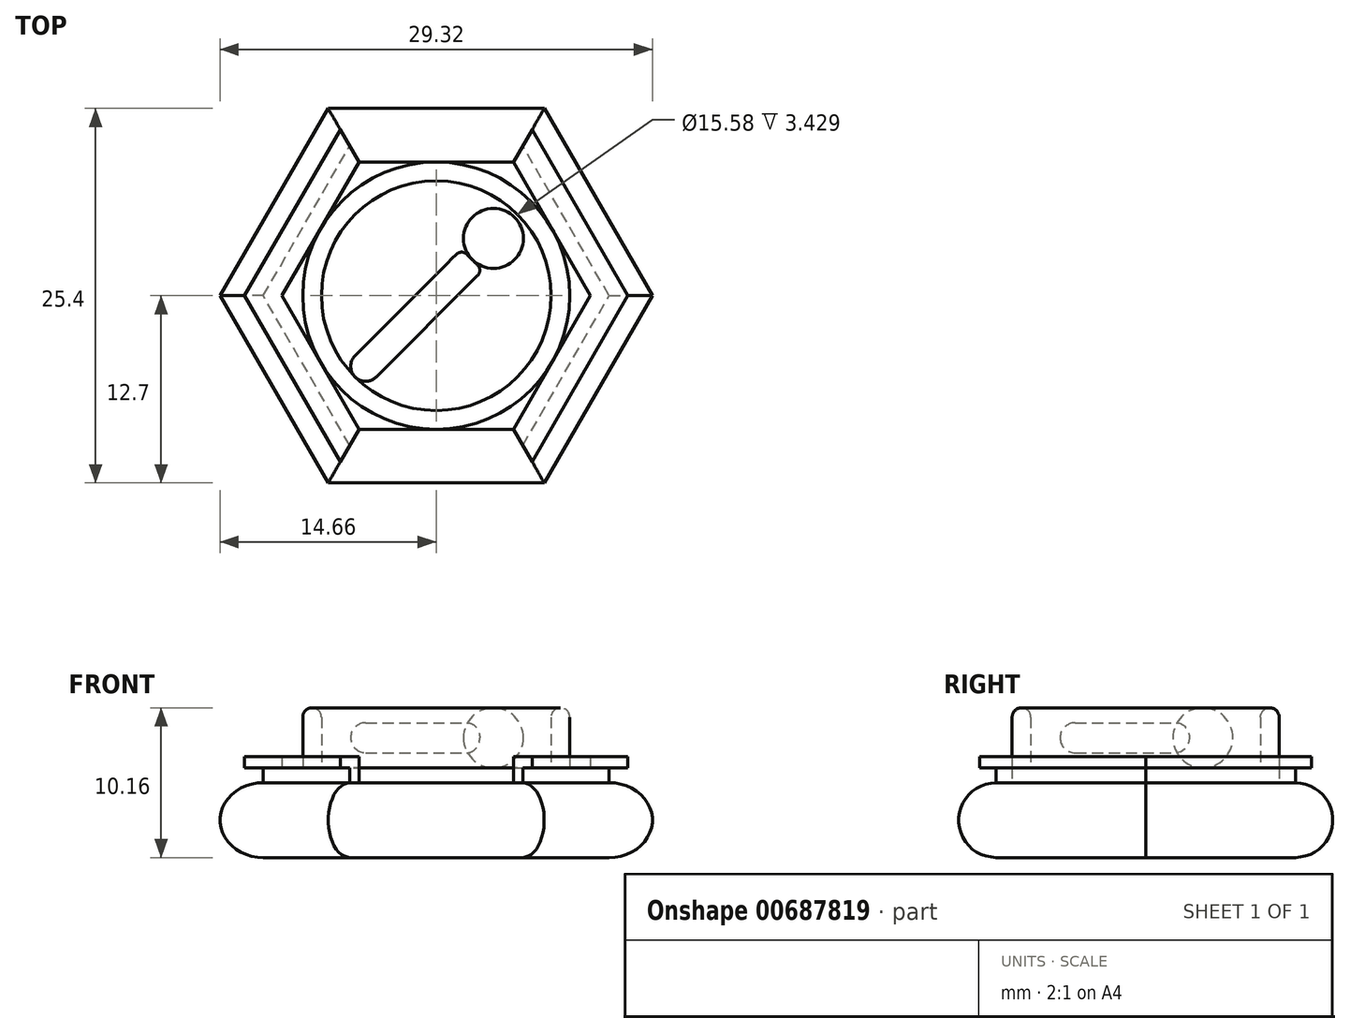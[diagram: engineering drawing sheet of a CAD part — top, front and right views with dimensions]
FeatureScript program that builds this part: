
annotation { "Feature Type Name" : "Feature", "Feature Type Description" : "" }
export const myFeature = defineFeature(function(context is Context, id is Id, definition is map)
    precondition{}
    {
        {
            var Q0;
            Q0=qCreatedBy(makeId("Front.planeOp"),FACE);
            var sketch = newSketch(context, id + "F0", { "sketchPlane" : qUnion([Q0])});
            skLineSegment(sketch, "E0", {"start": v(0, 0) * mm, "end": v(-12.7, 0) * mm});
            skLineSegment(sketch, "E1", {"start": v(-12.7, 0) * mm, "end": v(-12.7, 5.08) * mm, "construction": true});
            skLineSegment(sketch, "E2", {"start": v(12.7, 5.08) * mm, "end": v(12.7, 0) * mm, "construction": true});
            skLineSegment(sketch, "E3", {"start": v(12.7, 0) * mm, "end": v(0, 0) * mm});
            skArc(sketch, "E4", {"start": v(12.7, 0) * mm, "mid": v(15.24, 2.54) * mm, "end": v(12.7, 5.08) * mm});
            skArc(sketch, "E5", {"start": v(-12.7, 5.08) * mm, "mid": v(-15.24, 2.54) * mm, "end": v(-12.7, 0) * mm});
            skLineSegment(sketch, "E6", {"start": v(0, 0) * mm, "end": v(0, 5.08) * mm, "construction": true});
            skLineSegment(sketch, "E7", {"start": v(12.7, 2.54) * mm, "end": v(15.24, 2.54) * mm, "construction": true});
            skLineSegment(sketch, "E8", {"start": v(-12.7, 5.08) * mm, "end": v(12.7, 5.08) * mm});
            skPoint(sketch, "E9", {"position": v(0, 5.08) * mm});
            skSolve(sketch);
        }
        {
            var Q0;
            Q0=qSketchRegion(id+"F0",true);
            extrude(context, id + "F1", {"entities" : qUnion([Q0]), "endBound" : BoundingType.SYMMETRIC, "depth" : 25.4 * mm, "offsetDistance" : 25.4 * mm});
        }
        {
            var Q0;
            Q0=qCreatedBy(makeId("Right.planeOp"),FACE);
            var sketch = newSketch(context, id + "F2", { "sketchPlane" : qUnion([Q0])});
            skLineSegment(sketch, "E10", {"start": v(0, 0) * mm, "end": v(-10.16, 0) * mm, "construction": true});
            skLineSegment(sketch, "E11", {"start": v(0, 0) * mm, "end": v(10.16, 0) * mm, "construction": true});
            skLineSegment(sketch, "E12", {"start": v(-10.16, 0) * mm, "end": v(-10.16, 5.08) * mm, "construction": true});
            skLineSegment(sketch, "E13", {"start": v(10.16, 0) * mm, "end": v(10.16, 5.08) * mm, "construction": true});
            skArc(sketch, "E14", {"start": v(10.16, 0) * mm, "mid": v(12.7, 2.54) * mm, "end": v(10.16, 5.08) * mm});
            skArc(sketch, "E15", {"start": v(-10.16, 5.08) * mm, "mid": v(-12.7, 2.54) * mm, "end": v(-10.16, 0) * mm});
            skLineSegment(sketch, "E16", {"start": v(0, 0) * mm, "end": v(0, 5.08) * mm, "construction": true});
            skLineSegment(sketch, "E17", {"start": v(29.21, 5.08) * mm, "end": v(29.21, 0) * mm});
            skLineSegment(sketch, "E18", {"start": v(-29.21, 5.08) * mm, "end": v(-29.21, 0) * mm});
            skLineSegment(sketch, "E19", {"start": v(-10.16, 0) * mm, "end": v(-29.21, 0) * mm});
            skLineSegment(sketch, "E20", {"start": v(-10.16, 2.54) * mm, "end": v(-12.7, 2.54) * mm, "construction": true});
            skLineSegment(sketch, "E21", {"start": v(29.21, 0) * mm, "end": v(10.16, 0) * mm});
            skLineSegment(sketch, "E22", {"start": v(0, 0) * mm, "end": v(0, 0) * mm});
            skLineSegment(sketch, "E23", {"start": v(10.16, 5.08) * mm, "end": v(-10.16, 5.08) * mm, "construction": true});
            skLineSegment(sketch, "E24", {"start": v(29.21, 5.08) * mm, "end": v(10.16, 5.08) * mm});
            skLineSegment(sketch, "E25", {"start": v(-29.21, 5.08) * mm, "end": v(-10.16, 5.08) * mm});
            skSolve(sketch);
        }
        {
            var Q0;
            Q0=qSketchRegion(id+"F2",true);
            extrude(context, id + "F3", {"entities" : qUnion([Q0]), "operationType" : NewBodyOperationType.REMOVE, "endBound" : BoundingType.SYMMETRIC, "depth" : 50.8 * mm, "offsetDistance" : 25.4 * mm});
        }
        {
            var Q0;
            Q0=sQuery(id+"F0.wireOp",EDGE,"E6");
            cPlane(context, id + "F4", {"entities" : qUnion([Q0]), "cplaneType" : CPlaneType.LINE_ANGLE, "offset" : 25.4 * mm, "angle" : 120 * degree, "width" : 152.4 * mm, "height" : 152.4 * mm});
        }
        {
            var Q0;
            Q0=qCreatedBy(id+"F4.planeOp",FACE);
            var sketch = newSketch(context, id + "F5", { "sketchPlane" : qUnion([Q0])});
            skLineSegment(sketch, "E26", {"start": v(0, 0) * mm, "end": v(-10.16, 0) * mm, "construction": true});
            skLineSegment(sketch, "E27", {"start": v(0, 0) * mm, "end": v(10.16, 0) * mm, "construction": true});
            skLineSegment(sketch, "E28", {"start": v(-10.16, 0) * mm, "end": v(-10.16, 5.08) * mm, "construction": true});
            skLineSegment(sketch, "E29", {"start": v(10.16, 0) * mm, "end": v(10.16, 5.08) * mm, "construction": true});
            skArc(sketch, "E30", {"start": v(10.16, 0) * mm, "mid": v(12.7, 2.54) * mm, "end": v(10.16, 5.08) * mm});
            skArc(sketch, "E31", {"start": v(-10.16, 5.08) * mm, "mid": v(-12.7, 2.54) * mm, "end": v(-10.16, 0) * mm});
            skLineSegment(sketch, "E32", {"start": v(0, 0) * mm, "end": v(0, 5.08) * mm, "construction": true});
            skLineSegment(sketch, "E33", {"start": v(29.21, 5.08) * mm, "end": v(29.21, 0) * mm});
            skLineSegment(sketch, "E34", {"start": v(-29.21, 5.08) * mm, "end": v(-29.21, 0) * mm});
            skLineSegment(sketch, "E35", {"start": v(-10.16, 0) * mm, "end": v(-29.21, 0) * mm});
            skLineSegment(sketch, "E36", {"start": v(-10.16, 2.54) * mm, "end": v(-12.7, 2.54) * mm, "construction": true});
            skLineSegment(sketch, "E37", {"start": v(29.21, 0) * mm, "end": v(10.16, 0) * mm});
            skLineSegment(sketch, "E38", {"start": v(0, 0) * mm, "end": v(0, 0) * mm});
            skLineSegment(sketch, "E39", {"start": v(10.16, 5.08) * mm, "end": v(-10.16, 5.08) * mm, "construction": true});
            skLineSegment(sketch, "E40", {"start": v(29.21, 5.08) * mm, "end": v(10.16, 5.08) * mm});
            skLineSegment(sketch, "E41", {"start": v(-29.21, 5.08) * mm, "end": v(-10.16, 5.08) * mm});
            skSolve(sketch);
        }
        {
            var Q0;
            Q0=qSketchRegion(id+"F5",true);
            var Q1;
            Q1=sQuery(id+"FHUch5MhYWofbFd_1.wireOp",EDGE,"UJUXWhbe-ns99-R938-MBjs-qnEI7qI75ZtX");
            var Q2;
            Q2=sQuery(id+"FHUch5MhYWofbFd_1.wireOp",EDGE,"TGRI2bbO-5mKc-ZYGL-RI2u-ax8UZepCr2S6");
            var Q3;
            Q3=sQuery(id+"FHUch5MhYWofbFd_1.wireOp",EDGE,"3EN97P5a-7fpQ-fkxS-kFIG-O94JdEreBvdc");
            var Q4;
            Q4=sQuery(id+"FHUch5MhYWofbFd_1.wireOp",EDGE,"BLXI86f6-p3FV-xg8e-vcjV-MuaEN1ZbEeBN");
            var Q5;
            Q5=sQuery(id+"FHUch5MhYWofbFd_1.wireOp",EDGE,"K6Pg9hkI-HhUm-eWt8-lgsy-rQcUfMNRkeRX");
            var Q6;
            Q6=sQuery(id+"FHUch5MhYWofbFd_1.wireOp",EDGE,"8MWXePed-qfWZ-9kiI-xQLn-RgFZeWpe4DeW");
            var Q7;
            Q7=sQuery(id+"FHUch5MhYWofbFd_1.wireOp",EDGE,"ujHeR1Bt-oqxH-zWrO-aF7a-1cGxx1oxEC4p");
            var Q8;
            Q8=sQuery(id+"FHUch5MhYWofbFd_1.wireOp",EDGE,"ezDig2bh-fpcZ-qdXg-hfEw-k3bdO8GFTHoY");
            var Q9;
            Q9=sQuery(id+"FHUch5MhYWofbFd_1.wireOp",EDGE,"TL3t9Hpy-tibO-WM6d-k033-ZjCVjvvUcohB");
            var Q10;
            Q10=sQuery(id+"FHUch5MhYWofbFd_1.wireOp",EDGE,"H6XLH3zd-cpDk-JRaX-qujs-Kg6a5HbhHDUq");
            var Q11;
            Q11=sQuery(id+"FHUch5MhYWofbFd_1.wireOp",EDGE,"XlrNxneH-uq2I-L97s-EfPg-StDvBexp0ezL");
            var Q12;
            Q12=sQuery(id+"FHUch5MhYWofbFd_1.wireOp",EDGE,"V9PWrxtB-5fyD-G3Op-kF2t-xwj5HEO20ic1");
            var Q13;
            Q13=sQuery(id+"FHUch5MhYWofbFd_1.wireOp",EDGE,"DBsLzJAx-6rkW-YoXi-OfuC-MLqgEexGkzpa");
            extrude(context, id + "F6", {"entities" : qUnion([Q0]), "operationType" : NewBodyOperationType.REMOVE, "surfaceEntities" : qUnion([Q1, Q2, Q3, Q4, Q5, Q6, Q7, Q8, Q9, Q10, Q11, Q12, Q13]), "endBound" : BoundingType.SYMMETRIC, "oppositeDirection" : true, "depth" : 50.8 * mm, "offsetDistance" : 25.4 * mm});
        }
        {
            var Q0;
            Q0=sQuery(id+"F0.wireOp",EDGE,"E6");
            cPlane(context, id + "F7", {"entities" : qUnion([Q0]), "cplaneType" : CPlaneType.LINE_ANGLE, "offset" : 25.4 * mm, "angle" : 60 * degree, "width" : 152.4 * mm, "height" : 152.4 * mm});
        }
        {
            var Q0;
            Q0=qCreatedBy(id+"F7.planeOp",FACE);
            var sketch = newSketch(context, id + "F8", { "sketchPlane" : qUnion([Q0])});
            skLineSegment(sketch, "E42", {"start": v(0, 0) * mm, "end": v(-10.16, 0) * mm, "construction": true});
            skLineSegment(sketch, "E43", {"start": v(0, 0) * mm, "end": v(10.16, 0) * mm, "construction": true});
            skLineSegment(sketch, "E44", {"start": v(-10.16, 0) * mm, "end": v(-10.16, 5.08) * mm, "construction": true});
            skLineSegment(sketch, "E45", {"start": v(10.16, 0) * mm, "end": v(10.16, 5.08) * mm, "construction": true});
            skArc(sketch, "E46", {"start": v(10.16, 0) * mm, "mid": v(12.7, 2.54) * mm, "end": v(10.16, 5.08) * mm});
            skArc(sketch, "E47", {"start": v(-10.16, 5.08) * mm, "mid": v(-12.7, 2.54) * mm, "end": v(-10.16, 0) * mm});
            skLineSegment(sketch, "E48", {"start": v(0, 0) * mm, "end": v(0, 5.08) * mm, "construction": true});
            skLineSegment(sketch, "E49", {"start": v(29.21, 5.08) * mm, "end": v(29.21, 0) * mm});
            skLineSegment(sketch, "E50", {"start": v(-29.21, 5.08) * mm, "end": v(-29.21, 0) * mm});
            skLineSegment(sketch, "E51", {"start": v(-10.16, 0) * mm, "end": v(-29.21, 0) * mm});
            skLineSegment(sketch, "E52", {"start": v(-10.16, 2.54) * mm, "end": v(-12.7, 2.54) * mm, "construction": true});
            skLineSegment(sketch, "E53", {"start": v(29.21, 0) * mm, "end": v(10.16, 0) * mm});
            skLineSegment(sketch, "E54", {"start": v(0, 0) * mm, "end": v(0, 0) * mm});
            skLineSegment(sketch, "E55", {"start": v(10.16, 5.08) * mm, "end": v(-10.16, 5.08) * mm, "construction": true});
            skLineSegment(sketch, "E56", {"start": v(29.21, 5.08) * mm, "end": v(10.16, 5.08) * mm});
            skLineSegment(sketch, "E57", {"start": v(-29.21, 5.08) * mm, "end": v(-10.16, 5.08) * mm});
            skSolve(sketch);
        }
        {
            var Q0;
            Q0=qSketchRegion(id+"F8",true);
            extrude(context, id + "F9", {"entities" : qUnion([Q0]), "operationType" : NewBodyOperationType.REMOVE, "endBound" : BoundingType.SYMMETRIC, "oppositeDirection" : true, "depth" : 50.8 * mm, "offsetDistance" : 25.4 * mm});
        }
        {
            var Q0;
            Q0=makeQuery(id+"FriaykctB5W3C7Q_1.boolean.opBoolean","SPLIT",FACE,{"disambiguationData":[TD([makeQuery(id+"F6.boolean.opBoolean","COPY",FACE,{"derivedFrom":makeQuery(id+"F6.opExtrude","SWEPT_FACE",FACE,{"disambiguationData":[OSD([sQuery(id+"F5.wireOp",EDGE,"E30")])]})})])],"derivedFrom":makeQuery(id+"F1.opExtrude","SWEPT_FACE",FACE,{"disambiguationData":[OSD([sQuery(id+"F0.wireOp",EDGE,"E8")])]})});
            var sketch = newSketch(context, id + "F10", { "sketchPlane" : qUnion([Q0])});
            skLineSegment(sketch, "E58", {"start": v(5.87, 10.16) * mm, "end": v(6.5, 11.26) * mm});
            skLineSegment(sketch, "E59", {"start": v(6.5, 11.26) * mm, "end": v(13, 0) * mm});
            skLineSegment(sketch, "E60", {"start": v(13, 0) * mm, "end": v(6.5, -11.26) * mm});
            skLineSegment(sketch, "E61", {"start": v(-5.87, 10.16) * mm, "end": v(-6.5, 11.26) * mm});
            skLineSegment(sketch, "E62", {"start": v(-6.5, 11.26) * mm, "end": v(-13, 0) * mm});
            skLineSegment(sketch, "E63", {"start": v(-13, 0) * mm, "end": v(-6.5, -11.26) * mm});
            skLineSegment(sketch, "E64", {"start": v(-6.5, -11.26) * mm, "end": v(-5.87, -10.16) * mm});
            skLineSegment(sketch, "E65", {"start": v(6.5, -11.26) * mm, "end": v(5.87, -10.16) * mm});
            skLineSegment(sketch, "E66", {"start": v(5.23, 9.06) * mm, "end": v(10.46, 0) * mm});
            skLineSegment(sketch, "E67", {"start": v(10.46, 0) * mm, "end": v(5.23, -9.06) * mm});
            skLineSegment(sketch, "E68", {"start": v(5.23, -9.06) * mm, "end": v(5.87, -10.16) * mm});
            skLineSegment(sketch, "E69", {"start": v(0, 0) * mm, "end": v(5.23, 9.06) * mm, "construction": true});
            skLineSegment(sketch, "E70", {"start": v(5.23, 9.06) * mm, "end": v(5.87, 10.16) * mm});
            skLineSegment(sketch, "E71", {"start": v(0, 0) * mm, "end": v(-5.23, 9.06) * mm, "construction": true});
            skLineSegment(sketch, "E72", {"start": v(-5.23, 9.06) * mm, "end": v(-5.87, 10.16) * mm});
            skLineSegment(sketch, "E73", {"start": v(-5.23, 9.06) * mm, "end": v(-10.46, 0) * mm});
            skLineSegment(sketch, "E74", {"start": v(-10.46, 0) * mm, "end": v(-5.23, -9.06) * mm});
            skLineSegment(sketch, "E75", {"start": v(-5.23, -9.06) * mm, "end": v(-5.87, -10.16) * mm});
            skLineSegment(sketch, "E76", {"start": v(-5.23, -9.06) * mm, "end": v(5.23, -9.06) * mm});
            skLineSegment(sketch, "E77", {"start": v(-5.23, 9.06) * mm, "end": v(5.23, 9.06) * mm});
            skSolve(sketch);
        }
        {
            var Q0;
            Q0=makeQuery(id+"F10.imprint","IMPRINT",FACE,{"disambiguationData":[TD([[makeQuery(id+"F10.imprint","IMPRINT",EDGE,{"derivedFrom":sQuery(id+"F10.wireOp",EDGE,"E72")}),1.0]])]});
            var Q1;
            Q1=makeQuery(id+"F10.imprint","IMPRINT",FACE,{"disambiguationData":[TD([[makeQuery(id+"F10.imprint","IMPRINT",EDGE,{"derivedFrom":sQuery(id+"F10.wireOp",EDGE,"E61")}),1.0]])]});
            var Q2;
            Q2=makeQuery(id+"F10.imprint","IMPRINT",FACE,{"disambiguationData":[TD([[makeQuery(id+"F10.imprint","IMPRINT",EDGE,{"derivedFrom":sQuery(id+"F10.wireOp",EDGE,"E66")}),1.0]])]});
            var Q3;
            Q3=makeQuery(id+"F10.imprint","IMPRINT",FACE,{"disambiguationData":[TD([[makeQuery(id+"F10.imprint","IMPRINT",EDGE,{"derivedFrom":sQuery(id+"F10.wireOp",EDGE,"E58")}),-1.0]])]});
            extrude(context, id + "F11", {"entities" : qUnion([Q0, Q1, Q2, Q3]), "operationType" : NewBodyOperationType.ADD, "depth" : 1.78 * mm, "offsetDistance" : 25.4 * mm});
        }
        {
            var Q0;
            Q0=makeQuery(id+"F10.imprint","IMPRINT",FACE,{"disambiguationData":[TD([[makeQuery(id+"F10.imprint","IMPRINT",EDGE,{"derivedFrom":sQuery(id+"F10.wireOp",EDGE,"E58")}),-1.0]])]});
            var Q1;
            Q1=makeQuery(id+"F10.imprint","IMPRINT",FACE,{"disambiguationData":[TD([[makeQuery(id+"F10.imprint","IMPRINT",EDGE,{"derivedFrom":sQuery(id+"F10.wireOp",EDGE,"E61")}),1.0]])]});
            extrude(context, id + "F12", {"entities" : qUnion([Q0, Q1]), "operationType" : NewBodyOperationType.REMOVE, "depth" : 1.02 * mm, "offsetDistance" : 25.4 * mm});
        }
        {
            var Q0;
            Q0=makeQuery(id+"F10.imprint","IMPRINT",FACE,{"disambiguationData":[TD([[makeQuery(id+"F10.imprint","IMPRINT",EDGE,{"derivedFrom":sQuery(id+"F10.wireOp",EDGE,"E66")}),-1.0]])]});
            extrude(context, id + "F13", {"entities" : qUnion([Q0]), "operationType" : NewBodyOperationType.ADD, "depth" : 1.02 * mm, "offsetDistance" : 25.4 * mm});
        }
        {
            var Q0;
            Q0=makeQuery(id+"F13.opExtrude","CAP_FACE",FACE,{"disambiguationData":[OSD([sQuery(id+"F10.wireOp",EDGE,"E66"),sQuery(id+"F10.wireOp",EDGE,"E67"),sQuery(id+"F10.wireOp",EDGE,"E73"),sQuery(id+"F10.wireOp",EDGE,"E74"),sQuery(id+"F10.wireOp",EDGE,"E76"),sQuery(id+"F10.wireOp",EDGE,"E77")])],"isStart":false});
            cPlane(context, id + "F14", {"entities" : qUnion([Q0]), "cplaneType" : CPlaneType.OFFSET, "offset" : 2.03 * mm, "width" : 152.4 * mm, "height" : 152.4 * mm});
        }
        {
            var Q0;
            Q0=qCreatedBy(id+"F14.planeOp",FACE);
            var sketch = newSketch(context, id + "F15", { "sketchPlane" : qUnion([Q0])});
            skCircle(sketch, "E78", {"center": v(0, 0) * mm, "radius": 9.06 * mm});
            skLineSegment(sketch, "E79", {"start": v(-7.85, 4.53) * mm, "end": v(-6.75, 3.9) * mm, "construction": true});
            skCircle(sketch, "E80", {"center": v(0, 0) * mm, "radius": 7.8 * mm});
            skLineSegment(sketch, "E81", {"start": v(-7.8, 0) * mm, "end": v(7.8, 0) * mm, "construction": true});
            skLineSegment(sketch, "E82", {"start": v(-6.75, -3.88) * mm, "end": v(1, 3.88) * mm, "construction": true});
            skLineSegment(sketch, "E83", {"start": v(3.88, 1) * mm, "end": v(-3.88, -6.75) * mm, "construction": true});
            skLineSegment(sketch, "E84", {"start": v(1, 3.88) * mm, "end": v(3.88, 6.75) * mm});
            skLineSegment(sketch, "E85", {"start": v(3.88, 1) * mm, "end": v(6.75, 3.88) * mm});
            skLineSegment(sketch, "E86", {"start": v(0, 0) * mm, "end": v(-1.44, 1.44) * mm, "construction": true});
            skLineSegment(sketch, "E87", {"start": v(0, 0) * mm, "end": v(1.44, -1.44) * mm, "construction": true});
            skLineSegment(sketch, "E88", {"start": v(3.88, 1) * mm, "end": v(4.24, 0.65) * mm, "construction": true});
            skLineSegment(sketch, "E89", {"start": v(4.24, 0.65) * mm, "end": v(7.11, 3.52) * mm, "construction": true});
            skLineSegment(sketch, "E90", {"start": v(7.11, 3.52) * mm, "end": v(6.75, 3.88) * mm, "construction": true});
            skLineSegment(sketch, "E91", {"start": v(3.88, 6.75) * mm, "end": v(3.52, 7.11) * mm, "construction": true});
            skLineSegment(sketch, "E92", {"start": v(3.52, 7.11) * mm, "end": v(0.65, 4.24) * mm, "construction": true});
            skLineSegment(sketch, "E93", {"start": v(0.65, 4.24) * mm, "end": v(1, 3.88) * mm, "construction": true});
            skLineSegment(sketch, "E94", {"start": v(3.88, 6.75) * mm, "end": v(6.75, 3.88) * mm});
            skLineSegment(sketch, "E95", {"start": v(1, 3.88) * mm, "end": v(6.75, 3.88) * mm});
            skLineSegment(sketch, "E96", {"start": v(3.88, 3.88) * mm, "end": v(3.88, 1) * mm, "construction": true});
            skLineSegment(sketch, "E97", {"start": v(3.88, 3.88) * mm, "end": v(3.88, 6.75) * mm, "construction": true});
            skCircle(sketch, "E98", {"center": v(3.88, 3.88) * mm, "radius": 2.03 * mm});
            skLineSegment(sketch, "E99", {"start": v(2.44, 2.44) * mm, "end": v(0, 0) * mm});
            skLineSegment(sketch, "E100", {"start": v(0, 0) * mm, "end": v(-5.5, -5.5) * mm});
            skLineSegment(sketch, "E101", {"start": v(1, 3.88) * mm, "end": v(1.73, 3.16) * mm});
            skLineSegment(sketch, "E102", {"start": v(1.73, 3.16) * mm, "end": v(2.44, 2.44) * mm});
            skLineSegment(sketch, "E103", {"start": v(2.44, 2.44) * mm, "end": v(3.16, 1.73) * mm});
            skLineSegment(sketch, "E104", {"start": v(3.16, 1.73) * mm, "end": v(3.88, 1) * mm});
            skLineSegment(sketch, "E105", {"start": v(1.73, 3.16) * mm, "end": v(-6.18, -4.74) * mm});
            skLineSegment(sketch, "E106", {"start": v(3.16, 1.73) * mm, "end": v(-4.68, -6.23) * mm});
            skSolve(sketch);
        }
        {
            var Q0;
            {var subQ0=sQuery(id+"F15.wireOp",EDGE,"E98");var subQ1=makeQuery(id+"F15.imprint","INTERSECT",VERTEX,{"derivedFrom":[sQuery(id+"F15.wireOp",EDGE,"E84"),subQ0]});Q0=makeQuery(id+"F15.imprint","IMPRINT",FACE,{"disambiguationData":[TD([[makeQuery(id+"F15.imprint","IMPRINT",EDGE,{"disambiguationData":[TD([[subQ1,1.0]])],"derivedFrom":subQ0}),1.0]])]});}
            var Q1;
            Q1=sQuery(id+"F15.wireOp",EDGE,"E95");
            revolve(context, id + "F16", {"entities" : qUnion([Q0]), "axis" : qUnion([Q1]), "revolveType" : RevolveType.FULL});
        }
        {
            var Q0;
            Q0=makeQuery(id+"F15.imprint","IMPRINT",FACE,{"disambiguationData":[TD([[makeQuery(id+"F15.imprint","IMPRINT",EDGE,{"derivedFrom":sQuery(id+"F15.wireOp",EDGE,"E99")}),-1.0]])]});
            var Q1;
            Q1=sQuery(id+"F15.wireOp",EDGE,"E100");
            revolve(context, id + "F17", {"entities" : qUnion([Q0]), "axis" : qUnion([Q1]), "revolveType" : RevolveType.FULL, "surfaceOperationType" : NewSurfaceOperationType.NEW});
        }
        {
            var Q0;
            Q0=makeQuery(id+"F17.opRevolve","SWEPT_EDGE",EDGE,{"disambiguationData":[OSD([sQuery(id+"F15.wireOp",EDGE,"E80"),sQuery(id+"F15.wireOp",EDGE,"E82")])]});
            fillet(context, id + "F18", {"entities" : qUnion([Q0]), "radius" : 1.02 * mm, "tangentPropagation" : true, "allowEdgeOverflow" : false});
        }
        {
            var Q0;
            Q0=makeQuery(id+"F17.opRevolve","SWEPT_EDGE",EDGE,{"disambiguationData":[OSD([sQuery(id+"F15.wireOp",EDGE,"E101"),sQuery(id+"F15.wireOp",EDGE,"E102"),sQuery(id+"F15.wireOp",EDGE,"E105")])]});
            fillet(context, id + "F19", {"entities" : qUnion([Q0]), "radius" : 0.5 * mm, "tangentPropagation" : true, "allowEdgeOverflow" : false});
        }
        {
            var Q0;
            Q0=makeQuery(id+"F15.imprint","IMPRINT",FACE,{"disambiguationData":[TD([[makeQuery(id+"F15.imprint","IMPRINT",EDGE,{"derivedFrom":sQuery(id+"F15.wireOp",EDGE,"E78")}),1.0]])]});
            extrude(context, id + "F20", {"entities" : qUnion([Q0]), "endBound" : BoundingType.SYMMETRIC, "depth" : 4.06 * mm, "offsetDistance" : 25.4 * mm});
        }
        {
            var Q0;
            Q0=makeQuery(id+"F20.opExtrude","CAP_EDGE",EDGE,{"disambiguationData":[OSD([sQuery(id+"F15.wireOp",EDGE,"E78")])],"isStart":false});
            fillet(context, id + "F21", {"entities" : qUnion([Q0]), "radius" : 0.64 * mm, "tangentPropagation" : true, "allowEdgeOverflow" : false});
        }
        {
            var Q0;
            Q0=makeQuery(id+"F20.opExtrude","CAP_EDGE",EDGE,{"disambiguationData":[OSD([sQuery(id+"F15.wireOp",EDGE,"E80")])],"isStart":false});
            fillet(context, id + "F22", {"entities" : qUnion([Q0]), "radius" : 0.64 * mm, "tangentPropagation" : true, "allowEdgeOverflow" : false});
        }
    });
